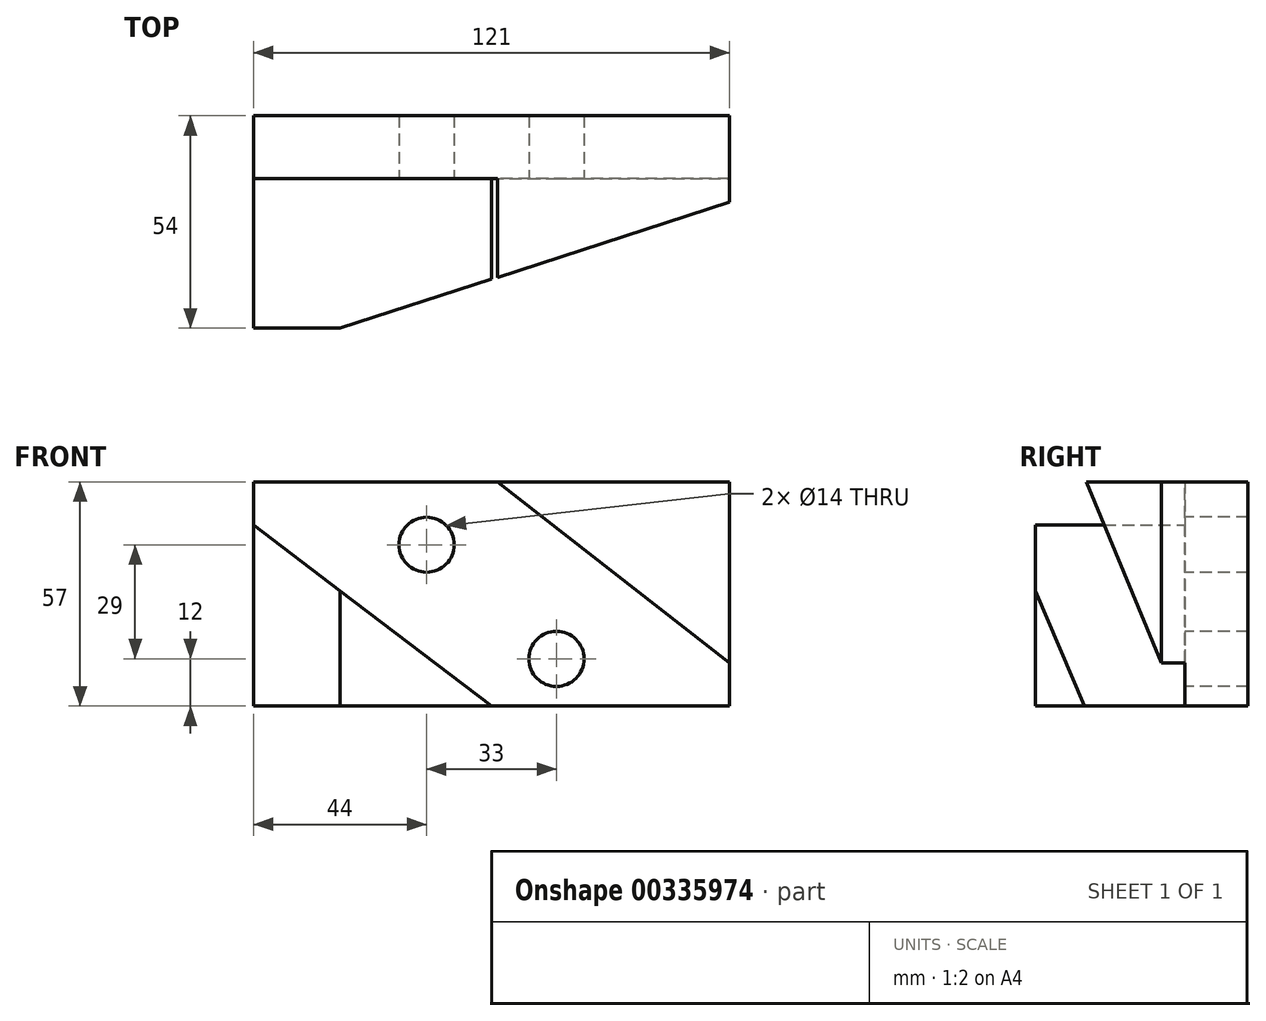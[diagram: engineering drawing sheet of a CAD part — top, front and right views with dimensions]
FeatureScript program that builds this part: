
annotation { "Feature Type Name" : "Feature", "Feature Type Description" : "" }
export const myFeature = defineFeature(function(context is Context, id is Id, definition is map)
    precondition{}
    {
        {
            var Q0;
            Q0=qCreatedBy(makeId("Top.planeOp"),FACE);
            var sketch = newSketch(context, id + "F0", { "sketchPlane" : qUnion([Q0])});
            skLineSegment(sketch, "E0.bottom", {"start": v(-60.5, 0) * mm, "end": v(60.5, 0) * mm});
            skLineSegment(sketch, "E0.top", {"start": v(-60.5, 16) * mm, "end": v(60.5, 16) * mm});
            skLineSegment(sketch, "E0.left", {"start": v(-60.5, 0) * mm, "end": v(-60.5, 16) * mm});
            skLineSegment(sketch, "E0.right", {"start": v(60.5, 0) * mm, "end": v(60.5, 16) * mm});
            skSolve(sketch);
        }
        {
            var Q0;
            Q0=makeQuery(id+"F0.imprint","IMPRINT",FACE,{"disambiguationData":[TD([[makeQuery(id+"F0.imprint","IMPRINT",EDGE,{"derivedFrom":sQuery(id+"F0.wireOp",EDGE,"E0.bottom")}),1.0]])]});
            extrude(context, id + "F1", {"entities" : qUnion([Q0]), "depth" : 57 * mm});
        }
        {
            var Q0;
            Q0=makeQuery(id+"F1.opExtrude","SWEPT_FACE",FACE,{"disambiguationData":[OSD([sQuery(id+"F0.wireOp",EDGE,"E0.bottom")])]});
            var sketch = newSketch(context, id + "F2", { "sketchPlane" : qUnion([Q0])});
            skLineSegment(sketch, "E1", {"start": v(-60.5, 0) * mm, "end": v(-60.5, 46) * mm});
            skLineSegment(sketch, "E2", {"start": v(-60.5, 46) * mm, "end": v(0, 0) * mm});
            skLineSegment(sketch, "E3", {"start": v(0, 0) * mm, "end": v(-60.5, 0) * mm});
            skLineSegment(sketch, "E4", {"start": v(-38.5, 29.27) * mm, "end": v(-38.5, 0) * mm});
            skLineSegment(sketch, "E5", {"start": v(1.5, 57) * mm, "end": v(60.5, 57) * mm});
            skLineSegment(sketch, "E6", {"start": v(60.5, 57) * mm, "end": v(60.5, 11) * mm});
            skLineSegment(sketch, "E7", {"start": v(60.5, 11) * mm, "end": v(1.5, 57) * mm});
            skCircle(sketch, "E8", {"center": v(-16.5, 41) * mm, "radius": 7 * mm});
            skCircle(sketch, "E9", {"center": v(16.5, 12) * mm, "radius": 7 * mm});
            skSolve(sketch);
        }
        {
            var Q0;
            Q0=makeQuery(id+"F2.imprint","IMPRINT",FACE,{"disambiguationData":[TD([[makeQuery(id+"F2.imprint","IMPRINT",EDGE,{"derivedFrom":sQuery(id+"F2.wireOp",EDGE,"E8")}),1.0]])]});
            var Q1;
            Q1=makeQuery(id+"F2.imprint","IMPRINT",FACE,{"disambiguationData":[TD([[makeQuery(id+"F2.imprint","IMPRINT",EDGE,{"derivedFrom":sQuery(id+"F2.wireOp",EDGE,"E9")}),1.0]])]});
            extrude(context, id + "F3", {"entities" : qUnion([Q0, Q1]), "operationType" : NewBodyOperationType.REMOVE, "endBound" : BoundingType.THROUGH_ALL, "oppositeDirection" : true, "depth" : 25 * mm});
        }
        {
            var Q0;
            {var subQ0=sQuery(id+"F2.wireOp",EDGE,"E1");Q0=makeQuery(id+"F2.imprint","IMPRINT",FACE,{"disambiguationData":[TD([[makeQuery(id+"F2.imprint","IMPRINT",EDGE,{"derivedFrom":subQ0}),1.0]])]});}
            var Q1;
            {var subQ3=sQuery(id+"F2.wireOp",EDGE,"E4");Q1=makeQuery(id+"F2.imprint","IMPRINT",FACE,{"disambiguationData":[TD([[makeQuery(id+"F2.imprint","IMPRINT",EDGE,{"derivedFrom":subQ3}),1.0]])]});}
            extrude(context, id + "F4", {"entities" : qUnion([Q0, Q1]), "operationType" : NewBodyOperationType.ADD, "depth" : 38 * mm});
        }
        {
            var Q0;
            Q0=makeQuery(id+"F2.imprint","IMPRINT",FACE,{"disambiguationData":[TD([[makeQuery(id+"F2.imprint","IMPRINT",EDGE,{"derivedFrom":sQuery(id+"F2.wireOp",EDGE,"E5")}),-1.0]])]});
            extrude(context, id + "F5", {"entities" : qUnion([Q0]), "operationType" : NewBodyOperationType.ADD, "depth" : 38 * mm});
        }
        {
            var Q0;
            {var subQ0=sQuery(id+"F0.wireOp",EDGE,"E0.bottom");var subQ1=makeQuery(id+"F1.opExtrude","CAP_EDGE",EDGE,{"disambiguationData":[OSD([subQ0])],"isStart":false});var subQ2=sQuery(id+"F0.wireOp",EDGE,"E0.left");var subQ3=sQuery(id+"F2.wireOp",EDGE,"E5");Q0=makeQuery(id+"FqPymqDn3PPWIpx_1.boolean.opBoolean","MERGE",FACE,{"derivedFrom":[makeQuery(id+"F5.boolean.opBoolean","MERGE",FACE,{"derivedFrom":[makeQuery(id+"F1.opExtrude","CAP_FACE",FACE,{"disambiguationData":[OSD([subQ0,sQuery(id+"F0.wireOp",EDGE,"E0.top"),subQ2,sQuery(id+"F0.wireOp",EDGE,"E0.right")])],"isStart":false}),makeQuery(id+"F5.opExtrude","SWEPT_FACE",FACE,{"disambiguationData":[OSD([subQ3])]})]}),makeQuery(id+"FqPymqDn3PPWIpx_1.opExtrude","SWEPT_FACE",FACE,{"disambiguationData":[OSD([subQ0]),TDD([makeQuery(id+"F2.imprint","IMPRINT",EDGE,{"disambiguationData":[TD([[makeQuery(id+"F2.imprint","INTERSECT",VERTEX,{"derivedFrom":[makeQuery(id+"F1.opExtrude","SWEPT_EDGE",EDGE,{"disambiguationData":[OSD([subQ0,subQ2])]}),subQ1]}),-1.0]])],"derivedFrom":subQ1})])]})]});}
            var sketch = newSketch(context, id + "F6", { "sketchPlane" : qUnion([Q0])});
            skLineSegment(sketch, "E10", {"start": v(-60.5, -38) * mm, "end": v(-38.5, -38) * mm});
            skLineSegment(sketch, "E11", {"start": v(-38.5, -38) * mm, "end": v(60.5, -6) * mm});
            skLineSegment(sketch, "E12", {"start": v(60.5, -6) * mm, "end": v(60.5, 16) * mm});
            skLineSegment(sketch, "E13", {"start": v(60.5, 16) * mm, "end": v(-60.5, 16) * mm});
            skLineSegment(sketch, "E14", {"start": v(-60.5, 16) * mm, "end": v(-60.5, -38) * mm});
            skLineSegment(sketch, "E15.0", {"start": v(-60.5, -38) * mm, "end": v(0, -38) * mm});
            skLineSegment(sketch, "E16.0.0", {"start": v(0, 0) * mm, "end": v(-60.5, 0) * mm});
            skLineSegment(sketch, "E16.0.1", {"start": v(-60.5, 0) * mm, "end": v(-60.5, -38) * mm});
            skLineSegment(sketch, "E16.0.3", {"start": v(0, -38) * mm, "end": v(0, 0) * mm});
            skLineSegment(sketch, "E17.0.1", {"start": v(-60.5, 16) * mm, "end": v(-60.5, 0) * mm});
            skLineSegment(sketch, "E17.0.2", {"start": v(-60.5, 0) * mm, "end": v(1.5, 0) * mm});
            skLineSegment(sketch, "E17.0.3", {"start": v(1.5, 0) * mm, "end": v(1.5, -38) * mm});
            skLineSegment(sketch, "E17.0.4", {"start": v(1.5, -38) * mm, "end": v(60.5, -38) * mm});
            skLineSegment(sketch, "E17.0.5", {"start": v(60.5, -38) * mm, "end": v(60.5, 16) * mm});
            skSolve(sketch);
        }
        {
            var Q0;
            {var subQ0=sQuery(id+"F6.wireOp",EDGE,"E15.0");var subQ1=sQuery(id+"F6.wireOp",EDGE,"E11");var subQ2=makeQuery(id+"F6.imprint","INTERSECT",VERTEX,{"derivedFrom":[subQ1,subQ0]});Q0=makeQuery(id+"F6.imprint","IMPRINT",FACE,{"disambiguationData":[TD([[makeQuery(id+"F6.imprint","IMPRINT",EDGE,{"disambiguationData":[TD([[subQ2,-1.0]])],"derivedFrom":subQ1}),-1.0]])]});}
            var Q1;
            {var subQ5=sQuery(id+"F6.wireOp",EDGE,"E17.0.4");Q1=makeQuery(id+"F6.imprint","IMPRINT",FACE,{"disambiguationData":[TD([[makeQuery(id+"F6.imprint","IMPRINT",EDGE,{"derivedFrom":subQ5}),1.0]])]});}
            extrude(context, id + "F7", {"entities" : qUnion([Q0, Q1]), "operationType" : NewBodyOperationType.REMOVE, "endBound" : BoundingType.THROUGH_ALL, "oppositeDirection" : true, "depth" : 25 * mm});
        }
    });
